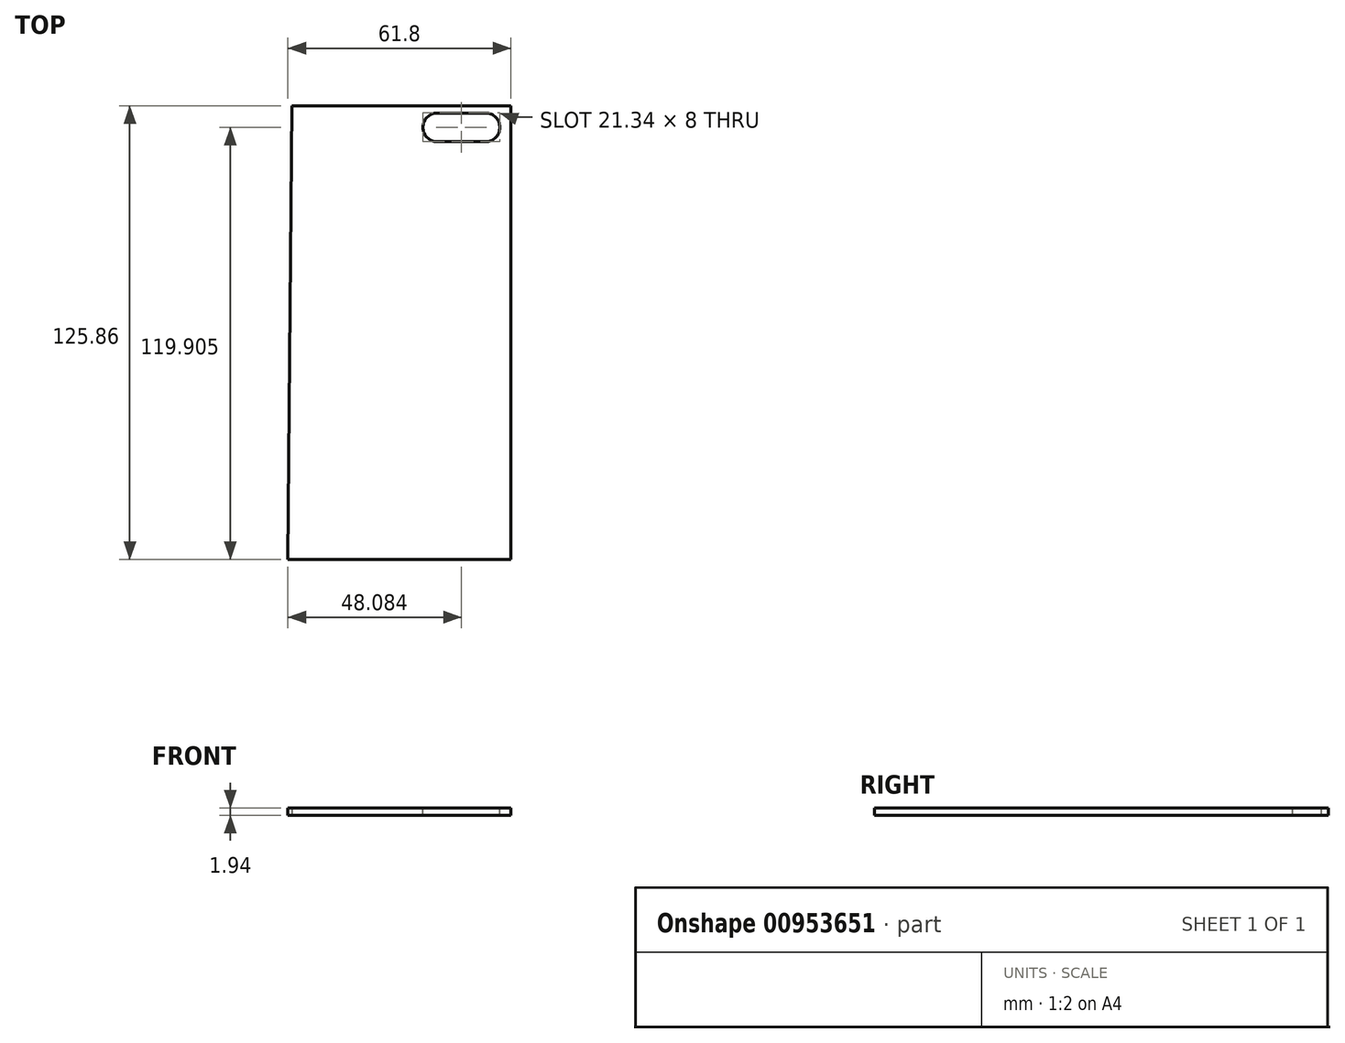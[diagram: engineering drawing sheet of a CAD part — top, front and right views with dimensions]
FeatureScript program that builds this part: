
annotation { "Feature Type Name" : "Feature", "Feature Type Description" : "" }
export const myFeature = defineFeature(function(context is Context, id is Id, definition is map)
    precondition{}
    {
        {
            var Q0;
            Q0=qCreatedBy(makeId("Top.planeOp"),FACE);
            var sketch = newSketch(context, id + "F0", { "sketchPlane" : qUnion([Q0])});
            skLineSegment(sketch, "E0", {"start": v(-32.98, 0) * mm, "end": v(27.72, 0) * mm});
            skLineSegment(sketch, "E1", {"start": v(-32.98, 0) * mm, "end": v(-34.08, -125.86) * mm});
            skLineSegment(sketch, "E2", {"start": v(27.72, 0) * mm, "end": v(27.72, -125.86) * mm});
            skLineSegment(sketch, "E3", {"start": v(27.72, -125.86) * mm, "end": v(-34.08, -125.86) * mm});
            skSolve(sketch);
        }
        {
            var Q0;
            Q0=makeQuery(id+"F0.imprint","IMPRINT",FACE,{"disambiguationData":[TD([[makeQuery(id+"F0.imprint","IMPRINT",EDGE,{"derivedFrom":sQuery(id+"F0.wireOp",EDGE,"E0")}),-1.0]])]});
            extrude(context, id + "F1", {"entities" : qUnion([Q0]), "depth" : 1.94 * mm, "offsetDistance" : 25.4 * mm});
        }
        {
            var Q0;
            Q0=makeQuery(id+"F1.opExtrude","CAP_FACE",FACE,{"disambiguationData":[OSD([sQuery(id+"F0.wireOp",EDGE,"E0"),sQuery(id+"F0.wireOp",EDGE,"E1"),sQuery(id+"F0.wireOp",EDGE,"E2"),sQuery(id+"F0.wireOp",EDGE,"E3")])],"isStart":false});
            var sketch = newSketch(context, id + "F2", { "sketchPlane" : qUnion([Q0])});
            skLineSegment(sketch, "E4", {"start": v(20.68, -4.3) * mm, "end": v(20.68, -1.96) * mm});
            skLineSegment(sketch, "E5", {"start": v(7.33, -4.3) * mm, "end": v(7.33, -1.96) * mm});
            skLineSegment(sketch, "E6", {"start": v(7.33, -1.96) * mm, "end": v(20.68, -1.96) * mm});
            skLineSegment(sketch, "E7", {"start": v(14, -1.96) * mm, "end": v(14, -4.3) * mm});
            skLineSegment(sketch, "E8", {"start": v(14, -4.3) * mm, "end": v(14, -1.96) * mm});
            skLineSegment(sketch, "E9", {"start": v(14, -1.96) * mm, "end": v(14, -9.95) * mm});
            skLineSegment(sketch, "E10", {"start": v(14, -9.95) * mm, "end": v(14, -1.96) * mm});
            skLineSegment(sketch, "E11", {"start": v(7.33, -4.3) * mm, "end": v(7.33, -9.95) * mm});
            skLineSegment(sketch, "E12", {"start": v(20.68, -4.3) * mm, "end": v(20.68, -9.95) * mm});
            skLineSegment(sketch, "E13", {"start": v(20.68, -9.95) * mm, "end": v(14.63, -9.95) * mm});
            skLineSegment(sketch, "E14", {"start": v(14.63, -9.95) * mm, "end": v(7.33, -9.95) * mm});
            skArc(sketch, "E15", {"start": v(7.33, -1.96) * mm, "mid": v(3.33, -5.95) * mm, "end": v(7.33, -9.95) * mm});
            skArc(sketch, "E16", {"start": v(20.68, -9.95) * mm, "mid": v(24.68, -5.95) * mm, "end": v(20.68, -1.96) * mm});
            skSolve(sketch);
        }
        {
            var Q0;
            Q0=makeQuery(id+"F2.imprint","IMPRINT",FACE,{"disambiguationData":[TD([[makeQuery(id+"F2.imprint","IMPRINT",EDGE,{"derivedFrom":sQuery(id+"F2.wireOp",EDGE,"E5")}),1.0]])]});
            var Q1;
            {var subQ7=sQuery(id+"F2.wireOp",EDGE,"E5");Q1=makeQuery(id+"F2.imprint","IMPRINT",FACE,{"disambiguationData":[TD([[makeQuery(id+"F2.imprint","IMPRINT",EDGE,{"derivedFrom":subQ7}),-1.0]])]});}
            var Q2;
            Q2=makeQuery(id+"F2.imprint","IMPRINT",FACE,{"disambiguationData":[TD([[makeQuery(id+"F2.imprint","IMPRINT",EDGE,{"derivedFrom":sQuery(id+"F2.wireOp",EDGE,"E4")}),-1.0]])]});
            var Q3;
            {var subQ5=sQuery(id+"F2.wireOp",EDGE,"E4");Q3=makeQuery(id+"F2.imprint","IMPRINT",FACE,{"disambiguationData":[TD([[makeQuery(id+"F2.imprint","IMPRINT",EDGE,{"derivedFrom":subQ5}),1.0]])]});}
            extrude(context, id + "F3", {"entities" : qUnion([Q0, Q1, Q2, Q3]), "operationType" : NewBodyOperationType.REMOVE, "oppositeDirection" : true, "depth" : 25.4 * mm, "offsetDistance" : 25.4 * mm});
        }
    });
